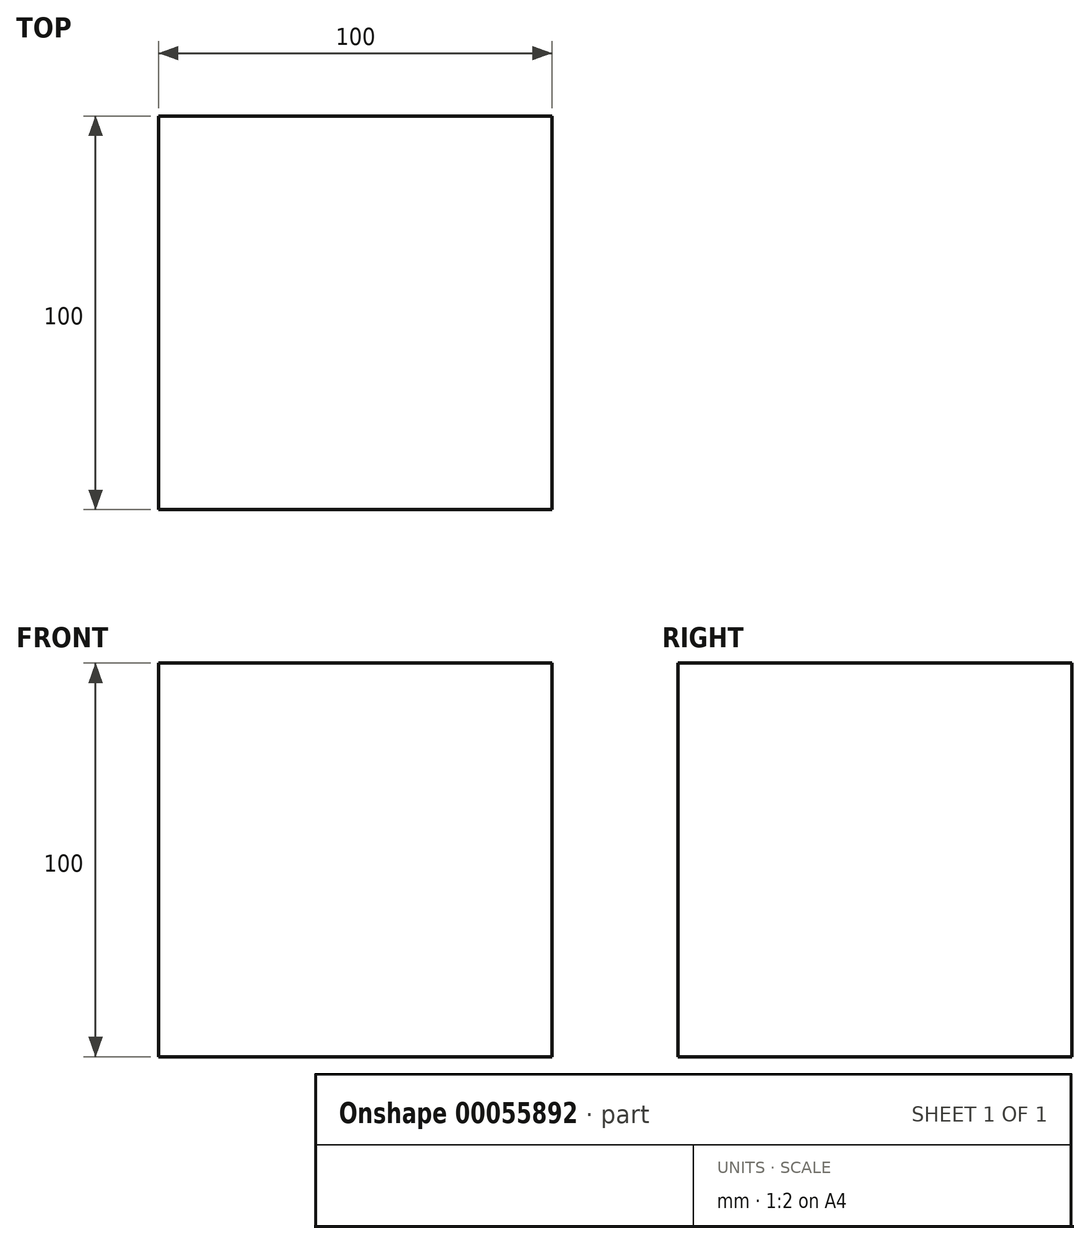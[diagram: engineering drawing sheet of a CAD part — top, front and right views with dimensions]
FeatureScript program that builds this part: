
annotation { "Feature Type Name" : "Feature", "Feature Type Description" : "" }
export const myFeature = defineFeature(function(context is Context, id is Id, definition is map)
    precondition{}
    {
        {
            var Q0;
            Q0=qCreatedBy(makeId("Front.planeOp"),FACE);
            var sketch = newSketch(context, id + "F0", { "sketchPlane" : qUnion([Q0])});
            skLineSegment(sketch, "E0.bottom", {"start": v(-47.6, 59.75) * mm, "end": v(52.4, 59.75) * mm});
            skLineSegment(sketch, "E0.top", {"start": v(-47.6, -40.25) * mm, "end": v(52.4, -40.25) * mm});
            skLineSegment(sketch, "E0.left", {"start": v(-47.6, 59.75) * mm, "end": v(-47.6, -40.25) * mm});
            skLineSegment(sketch, "E0.right", {"start": v(52.4, 59.75) * mm, "end": v(52.4, -40.25) * mm});
            skSolve(sketch);
        }
        {
            var Q0;
            Q0=makeQuery(id+"F0.imprint","IMPRINT",FACE,{"disambiguationData":[TD([[makeQuery(id+"F0.imprint","IMPRINT",EDGE,{"derivedFrom":sQuery(id+"F0.wireOp",EDGE,"E0.bottom")}),-1.0]])]});
            extrude(context, id + "F1", {"entities" : qUnion([Q0]), "depth" : 100 * mm});
        }
    });
